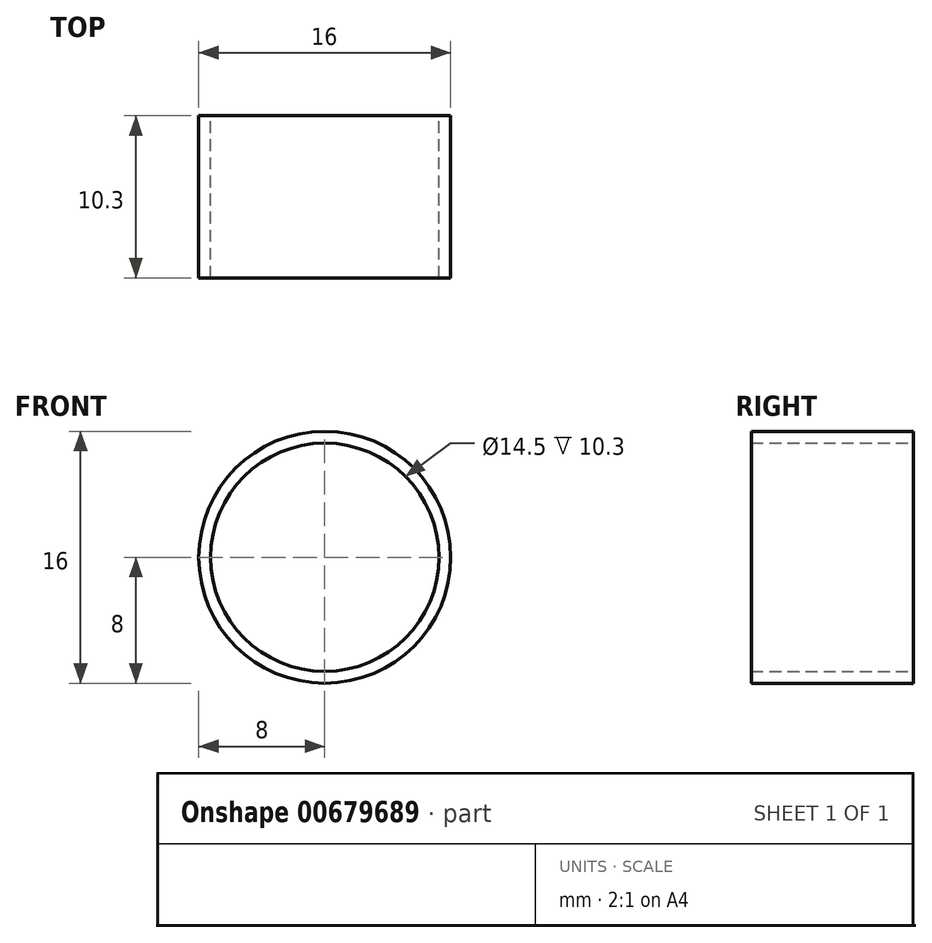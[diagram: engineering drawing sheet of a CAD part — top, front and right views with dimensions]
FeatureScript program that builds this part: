
annotation { "Feature Type Name" : "Feature", "Feature Type Description" : "" }
export const myFeature = defineFeature(function(context is Context, id is Id, definition is map)
    precondition{}
    {
        {
            var Q0;
            Q0=qCreatedBy(makeId("Front.planeOp"),FACE);
            var sketch = newSketch(context, id + "F0", { "sketchPlane" : qUnion([Q0])});
            skCircle(sketch, "E0", {"center": v(0, 0) * mm, "radius": 7.25 * mm});
            skCircle(sketch, "E1", {"center": v(0, 0) * mm, "radius": 8 * mm});
            skSolve(sketch);
        }
        {
            var Q0;
            Q0=makeQuery(id+"F0.imprint","IMPRINT",FACE,{"disambiguationData":[TD([[makeQuery(id+"F0.imprint","IMPRINT",EDGE,{"derivedFrom":sQuery(id+"F0.wireOp",EDGE,"E0")}),-1.0]])]});
            extrude(context, id + "F1", {"entities" : qUnion([Q0]), "endBound" : BoundingType.SYMMETRIC, "depth" : 10.3 * mm, "offsetDistance" : 25 * mm});
        }
    });
